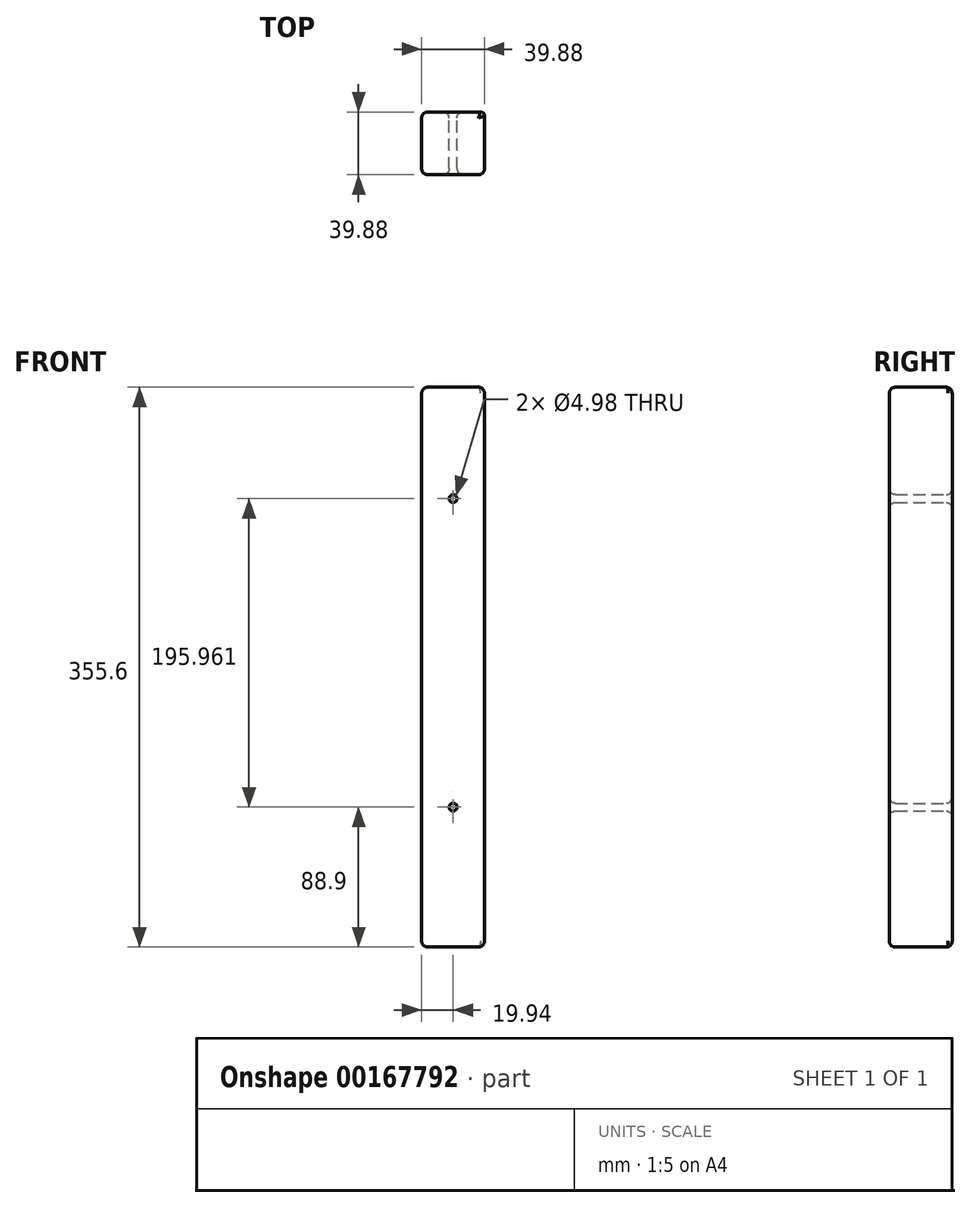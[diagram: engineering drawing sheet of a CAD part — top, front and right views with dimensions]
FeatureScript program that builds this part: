
annotation { "Feature Type Name" : "Feature", "Feature Type Description" : "" }
export const myFeature = defineFeature(function(context is Context, id is Id, definition is map)
    precondition{}
    {
        {
            var Q0;
            Q0=qCreatedBy(makeId("Front.planeOp"),FACE);
            var sketch = newSketch(context, id + "F0", { "sketchPlane" : qUnion([Q0])});
            skLineSegment(sketch, "E0.bottom", {"start": v(19.94, -177.8) * mm, "end": v(-19.94, -177.8) * mm});
            skLineSegment(sketch, "E0.top", {"start": v(19.94, 177.8) * mm, "end": v(-19.94, 177.8) * mm});
            skLineSegment(sketch, "E0.left", {"start": v(19.94, -177.8) * mm, "end": v(19.94, 177.8) * mm});
            skLineSegment(sketch, "E0.right", {"start": v(-19.94, -177.8) * mm, "end": v(-19.94, 177.8) * mm});
            skPoint(sketch, "E0.middle", {"position": v(0, 0) * mm});
            skCircle(sketch, "E1", {"center": v(0, 107.06) * mm, "radius": 2.49 * mm});
            skLineSegment(sketch, "E2", {"start": v(-19.94, -177.8) * mm, "end": v(-19.94, -101.6) * mm});
            skLineSegment(sketch, "E3", {"start": v(-19.94, -101.6) * mm, "end": v(19.94, -101.6) * mm});
            skCircle(sketch, "E4", {"center": v(0, -88.9) * mm, "radius": 2.49 * mm});
            skSolve(sketch);
        }
        {
            var Q0;
            Q0=qSketchRegion(id+"F0",true);
            extrude(context, id + "F1", {"entities" : qUnion([Q0]), "depth" : 39.88 * mm});
        }
        {
            var Q0;
            Q0=makeQuery(id+"F1.opExtrude","CAP_EDGE",EDGE,{"disambiguationData":[OSD([sQuery(id+"F0.wireOp",EDGE,"E0.right"),sQuery(id+"F0.wireOp",EDGE,"E2")])],"isStart":false});
            var Q1;
            Q1=makeQuery(id+"F1.opExtrude","CAP_EDGE",EDGE,{"disambiguationData":[OSD([sQuery(id+"F0.wireOp",EDGE,"E0.right"),sQuery(id+"F0.wireOp",EDGE,"E2")])],"isStart":true});
            var Q2;
            Q2=makeQuery(id+"F1.opExtrude","CAP_EDGE",EDGE,{"disambiguationData":[OSD([sQuery(id+"F0.wireOp",EDGE,"E1")])],"isStart":true});
            var Q3;
            Q3=makeQuery(id+"F1.opExtrude","CAP_EDGE",EDGE,{"disambiguationData":[OSD([sQuery(id+"F0.wireOp",EDGE,"E4")])],"isStart":true});
            var Q4;
            Q4=makeQuery(id+"F1.opExtrude","CAP_EDGE",EDGE,{"disambiguationData":[OSD([sQuery(id+"F0.wireOp",EDGE,"E4")])],"isStart":false});
            var Q5;
            Q5=makeQuery(id+"F1.opExtrude","CAP_EDGE",EDGE,{"disambiguationData":[OSD([sQuery(id+"F0.wireOp",EDGE,"E0.left")])],"isStart":false});
            var Q6;
            Q6=makeQuery(id+"F1.opExtrude","CAP_EDGE",EDGE,{"disambiguationData":[OSD([sQuery(id+"F0.wireOp",EDGE,"E1")])],"isStart":false});
            fillet(context, id + "F2", {"entities" : qUnion([Q0, Q1, Q2, Q3, Q4, Q5, Q6]), "radius" : 3.8 * mm, "tangentPropagation" : true, "allowEdgeOverflow" : false});
        }
        {
            var Q0;
            Q0=makeQuery(id+"F1.opExtrude","CAP_EDGE",EDGE,{"disambiguationData":[OSD([sQuery(id+"F0.wireOp",EDGE,"E0.top")])],"isStart":false});
            var Q1;
            Q1=makeQuery(id+"F1.opExtrude","SWEPT_EDGE",EDGE,{"disambiguationData":[OSD([sQuery(id+"F0.wireOp",EDGE,"E0.top"),sQuery(id+"F0.wireOp",EDGE,"E0.left")])]});
            var Q2;
            Q2=makeQuery(id+"F1.opExtrude","CAP_EDGE",EDGE,{"disambiguationData":[OSD([sQuery(id+"F0.wireOp",EDGE,"E0.top")])],"isStart":true});
            var Q3;
            Q3=makeQuery(id+"F1.opExtrude","SWEPT_EDGE",EDGE,{"disambiguationData":[OSD([sQuery(id+"F0.wireOp",EDGE,"E0.top"),sQuery(id+"F0.wireOp",EDGE,"E0.right")])]});
            var Q4;
            Q4=makeQuery(id+"F1.opExtrude","CAP_EDGE",EDGE,{"disambiguationData":[OSD([sQuery(id+"F0.wireOp",EDGE,"E0.bottom")])],"isStart":false});
            var Q5;
            Q5=makeQuery(id+"F1.opExtrude","SWEPT_EDGE",EDGE,{"disambiguationData":[OSD([sQuery(id+"F0.wireOp",EDGE,"E0.bottom"),sQuery(id+"F0.wireOp",EDGE,"E2")])]});
            var Q6;
            Q6=makeQuery(id+"F1.opExtrude","CAP_EDGE",EDGE,{"disambiguationData":[OSD([sQuery(id+"F0.wireOp",EDGE,"E0.bottom")])],"isStart":true});
            var Q7;
            Q7=makeQuery(id+"F1.opExtrude","SWEPT_EDGE",EDGE,{"disambiguationData":[OSD([sQuery(id+"F0.wireOp",EDGE,"E0.bottom"),sQuery(id+"F0.wireOp",EDGE,"E0.left")])]});
            fillet(context, id + "F3", {"entities" : qUnion([Q0, Q1, Q2, Q3, Q4, Q5, Q6, Q7]), "radius" : 3.8 * mm, "tangentPropagation" : true, "allowEdgeOverflow" : false});
        }
        {
            var Q0;
            Q0=makeQuery(id+"F1.opExtrude","CAP_EDGE",EDGE,{"disambiguationData":[OSD([sQuery(id+"F0.wireOp",EDGE,"E0.left")])],"isStart":true});
            fillet(context, id + "F4", {"entities" : qUnion([Q0]), "radius" : 2.54 * mm, "tangentPropagation" : true, "allowEdgeOverflow" : false});
        }
    });
